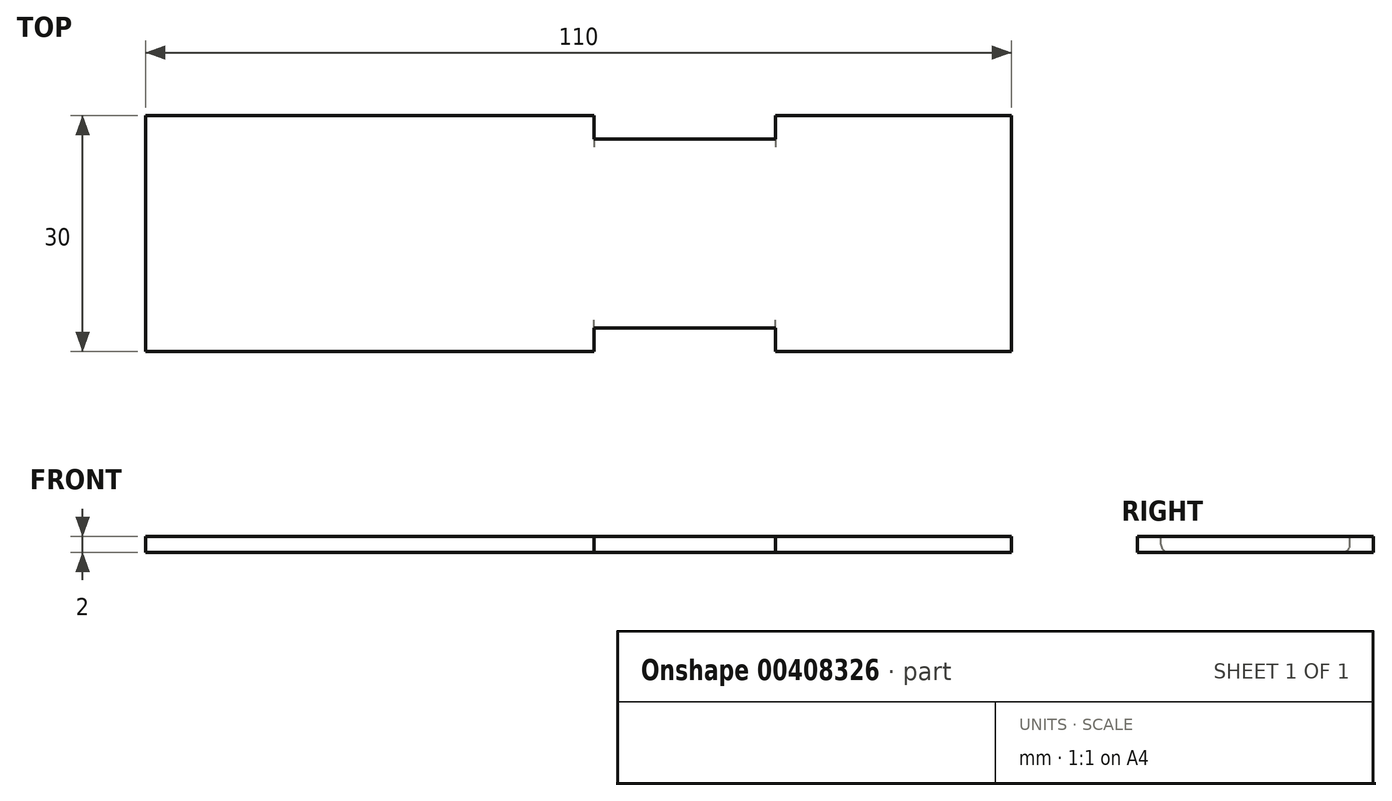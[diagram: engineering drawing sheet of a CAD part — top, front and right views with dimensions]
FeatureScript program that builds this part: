
annotation { "Feature Type Name" : "Feature", "Feature Type Description" : "" }
export const myFeature = defineFeature(function(context is Context, id is Id, definition is map)
    precondition{}
    {
        {
            var Q0;
            Q0=qCreatedBy(makeId("Top.planeOp"),FACE);
            var sketch = newSketch(context, id + "F0", { "sketchPlane" : qUnion([Q0])});
            skLineSegment(sketch, "E0.bottom", {"start": v(55, -15) * mm, "end": v(-55, -15) * mm});
            skLineSegment(sketch, "E0.top", {"start": v(55, 15) * mm, "end": v(-55, 15) * mm});
            skLineSegment(sketch, "E0.left", {"start": v(55, -15) * mm, "end": v(55, 15) * mm});
            skLineSegment(sketch, "E0.right", {"start": v(-55, -15) * mm, "end": v(-55, 15) * mm});
            skPoint(sketch, "E0.middle", {"position": v(0, 0) * mm});
            skSolve(sketch);
        }
        {
            var Q0;
            Q0=makeQuery(id+"F0.imprint","IMPRINT",FACE,{"disambiguationData":[TD([[makeQuery(id+"F0.imprint","IMPRINT",EDGE,{"derivedFrom":sQuery(id+"F0.wireOp",EDGE,"E0.bottom")}),-1.0]])]});
            extrude(context, id + "F1", {"entities" : qUnion([Q0]), "depth" : 2 * mm});
        }
        {
            var Q0;
            Q0=makeQuery(id+"F1.opExtrude","CAP_FACE",FACE,{"disambiguationData":[OSD([sQuery(id+"F0.wireOp",EDGE,"E0.bottom"),sQuery(id+"F0.wireOp",EDGE,"E0.top"),sQuery(id+"F0.wireOp",EDGE,"E0.left"),sQuery(id+"F0.wireOp",EDGE,"E0.right")])],"isStart":false});
            var sketch = newSketch(context, id + "F2", { "sketchPlane" : qUnion([Q0])});
            skLineSegment(sketch, "E1.bottom", {"start": v(25, 15) * mm, "end": v(2, 15) * mm});
            skLineSegment(sketch, "E1.top", {"start": v(25, 12) * mm, "end": v(2, 12) * mm});
            skLineSegment(sketch, "E1.left", {"start": v(25, 15) * mm, "end": v(25, 12) * mm});
            skLineSegment(sketch, "E1.right", {"start": v(2, 15) * mm, "end": v(2, 12) * mm});
            skLineSegment(sketch, "E2.MirrorCS", {"start": v(2, -15) * mm, "end": v(2, -12) * mm});
            skLineSegment(sketch, "E3.MirrorCS", {"start": v(25, -15) * mm, "end": v(2, -15) * mm});
            skLineSegment(sketch, "E4.MirrorCS", {"start": v(25, -12) * mm, "end": v(2, -12) * mm});
            skLineSegment(sketch, "E5.MirrorCS", {"start": v(25, -15) * mm, "end": v(25, -12) * mm});
            skSolve(sketch);
        }
        {
            var Q0;
            Q0 = qSketchRegion(id + "F2", true);
            extrude(context, id + "F3", {"entities" : qUnion([Q0]), "operationType" : NewBodyOperationType.REMOVE, "oppositeDirection" : true, "depth" : 25 * mm});
        }
        {
            var Q0;
            Q0=makeQuery(id+"F3.boolean.opBoolean","INTERSECT",EDGE,{"derivedFrom":[makeQuery(id+"F1.opExtrude","CAP_FACE",FACE,{"disambiguationData":[OSD([sQuery(id+"F0.wireOp",EDGE,"E0.bottom"),sQuery(id+"F0.wireOp",EDGE,"E0.top"),sQuery(id+"F0.wireOp",EDGE,"E0.left"),sQuery(id+"F0.wireOp",EDGE,"E0.right")])],"isStart":true}),makeQuery(id+"F3.opExtrude","SWEPT_FACE",FACE,{"disambiguationData":[OSD([sQuery(id+"F2.wireOp",EDGE,"E4.MirrorCS")])]})]});
            var Q1;
            Q1=makeQuery(id+"F3.boolean.opBoolean","INTERSECT",EDGE,{"derivedFrom":[makeQuery(id+"F1.opExtrude","CAP_FACE",FACE,{"disambiguationData":[OSD([sQuery(id+"F0.wireOp",EDGE,"E0.bottom"),sQuery(id+"F0.wireOp",EDGE,"E0.top"),sQuery(id+"F0.wireOp",EDGE,"E0.left"),sQuery(id+"F0.wireOp",EDGE,"E0.right")])],"isStart":true}),makeQuery(id+"F3.opExtrude","SWEPT_FACE",FACE,{"disambiguationData":[OSD([sQuery(id+"F2.wireOp",EDGE,"E1.top")])]})]});
            fillet(context, id + "F4", {"entities" : qUnion([Q0, Q1]), "radius" : 1 * mm, "tangentPropagation" : true, "allowEdgeOverflow" : false});
        }
    });
